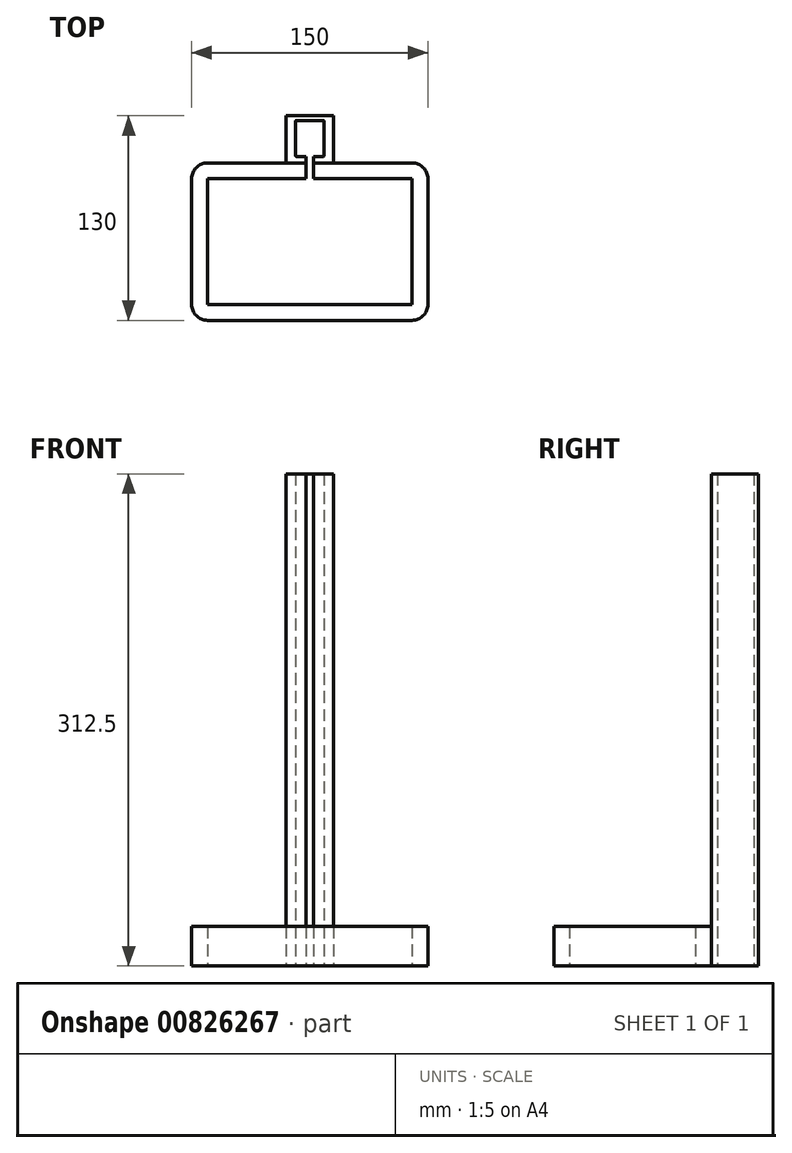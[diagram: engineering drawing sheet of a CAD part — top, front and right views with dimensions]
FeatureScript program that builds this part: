
annotation { "Feature Type Name" : "Feature", "Feature Type Description" : "" }
export const myFeature = defineFeature(function(context is Context, id is Id, definition is map)
    precondition{}
    {
        {
            var Q0;
            Q0=qCreatedBy(makeId("Top.planeOp"),FACE);
            var sketch = newSketch(context, id + "F0", { "sketchPlane" : qUnion([Q0])});
            skLineSegment(sketch, "E0.bottom", {"start": v(-65, 50) * mm, "end": v(65, 50) * mm});
            skLineSegment(sketch, "E0.top", {"start": v(-65, -50) * mm, "end": v(65, -50) * mm});
            skLineSegment(sketch, "E0.left", {"start": v(-75, 40) * mm, "end": v(-75, -40) * mm});
            skLineSegment(sketch, "E0.right", {"start": v(75, 40) * mm, "end": v(75, -40) * mm});
            skLineSegment(sketch, "E1", {"start": v(0, 0) * mm, "end": v(-75, 0) * mm, "construction": true});
            skLineSegment(sketch, "E2", {"start": v(0, 0) * mm, "end": v(0, -50) * mm, "construction": true});
            skLineSegment(sketch, "E3.bottom", {"start": v(-15, 80) * mm, "end": v(15, 80) * mm});
            skLineSegment(sketch, "E3.top", {"start": v(-15, 50) * mm, "end": v(15, 50) * mm});
            skLineSegment(sketch, "E3.left", {"start": v(-15, 80) * mm, "end": v(-15, 50) * mm});
            skLineSegment(sketch, "E3.right", {"start": v(15, 80) * mm, "end": v(15, 50) * mm});
            skLineSegment(sketch, "E4", {"start": v(0, 0) * mm, "end": v(0, 80) * mm, "construction": true});
            skLineSegment(sketch, "E5.bottom", {"start": v(-65, 40) * mm, "end": v(65, 40) * mm});
            skLineSegment(sketch, "E5.top", {"start": v(-65, -40) * mm, "end": v(65, -40) * mm});
            skLineSegment(sketch, "E5.left", {"start": v(-65, 40) * mm, "end": v(-65, -40) * mm});
            skLineSegment(sketch, "E5.right", {"start": v(65, 40) * mm, "end": v(65, -40) * mm});
            skLineSegment(sketch, "E6.bottom", {"start": v(-2.5, 59.58) * mm, "end": v(2.5, 59.58) * mm});
            skLineSegment(sketch, "E6.top", {"start": v(-2.5, 40) * mm, "end": v(2.5, 40) * mm});
            skLineSegment(sketch, "E6.left", {"start": v(-2.5, 59.58) * mm, "end": v(-2.5, 40) * mm});
            skLineSegment(sketch, "E6.right", {"start": v(2.5, 59.58) * mm, "end": v(2.5, 40) * mm});
            skLineSegment(sketch, "E7", {"start": v(0, 0) * mm, "end": v(-65, 0) * mm, "construction": true});
            skPoint(sketch, "E8.visualSharp", {"position": v(-75, 50) * mm});
            skArc(sketch, "E8.filletArc", {"start": v(-65, 50) * mm, "mid": v(-72.07, 47.07) * mm, "end": v(-75, 40) * mm});
            skPoint(sketch, "E9.visualSharp", {"position": v(75, 50) * mm});
            skArc(sketch, "E9.filletArc", {"start": v(75, 40) * mm, "mid": v(72.07, 47.07) * mm, "end": v(65, 50) * mm});
            skPoint(sketch, "E10.visualSharp", {"position": v(-75, -50) * mm});
            skArc(sketch, "E10.filletArc", {"start": v(-75, -40) * mm, "mid": v(-72.07, -47.07) * mm, "end": v(-65, -50) * mm});
            skPoint(sketch, "E11.visualSharp", {"position": v(75, -50) * mm});
            skArc(sketch, "E11.filletArc", {"start": v(65, -50) * mm, "mid": v(72.07, -47.07) * mm, "end": v(75, -40) * mm});
            skLineSegment(sketch, "E12", {"start": v(0, 0) * mm, "end": v(0, 40) * mm});
            skCircle(sketch, "E13", {"center": v(0, 69.7) * mm, "radius": 6 * mm});
            skLineSegment(sketch, "E14", {"start": v(-9, 54) * mm, "end": v(-9, 77) * mm});
            skLineSegment(sketch, "E15", {"start": v(-9, 77) * mm, "end": v(9, 77) * mm});
            skLineSegment(sketch, "E16", {"start": v(0, 79.25) * mm, "end": v(0, 80) * mm});
            skLineSegment(sketch, "E17", {"start": v(-9, 54) * mm, "end": v(9, 54) * mm});
            skLineSegment(sketch, "E18", {"start": v(9, 54) * mm, "end": v(9, 77) * mm});
            skLineSegment(sketch, "E19", {"start": v(0, 77) * mm, "end": v(0, 80) * mm});
            skSolve(sketch);
        }
        {
            var Q0;
            Q0=makeQuery(id+"F0.imprint","IMPRINT",FACE,{"disambiguationData":[TD([[makeQuery(id+"F0.imprint","IMPRINT",EDGE,{"derivedFrom":sQuery(id+"F0.wireOp",EDGE,"E0.top")}),1.0]])]});
            var Q1;
            {var subQ5=sQuery(id+"F0.wireOp",EDGE,"E6.top");Q1=makeQuery(id+"F0.imprint","IMPRINT",FACE,{"disambiguationData":[TD([[makeQuery(id+"F0.imprint","IMPRINT",EDGE,{"derivedFrom":subQ5}),1.0]])]});}
            var Q2;
            {var subQ0=sQuery(id+"F0.wireOp",EDGE,"l1MtYh9c-CzXV-YJr5-94RZ-eUTwZ6HwwpDR");Q2=makeQuery(id+"F0.imprint","IMPRINT",FACE,{"disambiguationData":[TD([[makeQuery(id+"F0.imprint","IMPRINT",EDGE,{"derivedFrom":subQ0}),1.0]])]});}
            extrude(context, id + "F1", {"entities" : qUnion([Q0, Q1, Q2]), "endBound" : BoundingType.SYMMETRIC, "depth" : 25 * mm, "offsetDistance" : 25 * mm});
        }
        {
            var Q0;
            Q0=makeQuery(id+"F0.imprint","IMPRINT",FACE,{"disambiguationData":[TD([[makeQuery(id+"F0.imprint","IMPRINT",EDGE,{"derivedFrom":sQuery(id+"F0.wireOp",EDGE,"E3.bottom")}),-1.0]])]});
            var Q1;
            {var subQ0=sQuery(id+"F0.wireOp",EDGE,"iEGK5Bb7-SoDk-IzIK-Jkqt-TQqyKEJhDGZO");Q1=makeQuery(id+"F0.imprint","IMPRINT",FACE,{"disambiguationData":[TD([[makeQuery(id+"F0.imprint","IMPRINT",EDGE,{"derivedFrom":subQ0}),1.0]])]});}
            extrude(context, id + "F2", {"entities" : qUnion([Q0, Q1]), "operationType" : NewBodyOperationType.ADD, "depth" : 300 * mm, "offsetDistance" : 25 * mm, "hasSecondDirection" : true, "secondDirectionOppositeDirection" : true, "secondDirectionDepth" : 12.5 * mm});
        }
        {
            var Q0;
            Q0=makeQuery(id+"F0.imprint","IMPRINT",FACE,{"disambiguationData":[TD([[makeQuery(id+"F0.imprint","IMPRINT",EDGE,{"derivedFrom":sQuery(id+"F0.wireOp",EDGE,"E13")}),1.0]])]});
            extrude(context, id + "F3", {"entities" : qUnion([Q0]), "operationType" : NewBodyOperationType.REMOVE, "depth" : 50 * mm, "offsetDistance" : 25 * mm});
        }
        {
            var Q0;
            Q0=makeQuery(id+"F2.opExtrude","SWEPT_EDGE",EDGE,{"disambiguationData":[OSD([sQuery(id+"F0.wireOp",EDGE,"E14"),sQuery(id+"F0.wireOp",EDGE,"E15")])]});
            var Q1;
            Q1=makeQuery(id+"F2.opExtrude","SWEPT_EDGE",EDGE,{"disambiguationData":[OSD([sQuery(id+"F0.wireOp",EDGE,"E15"),sQuery(id+"F0.wireOp",EDGE,"E18")])]});
            var Q2;
            Q2=makeQuery(id+"F2.opExtrude","SWEPT_EDGE",EDGE,{"disambiguationData":[OSD([sQuery(id+"F0.wireOp",EDGE,"E14"),sQuery(id+"F0.wireOp",EDGE,"E17")])]});
            var Q3;
            Q3=makeQuery(id+"F2.opExtrude","SWEPT_EDGE",EDGE,{"disambiguationData":[OSD([sQuery(id+"F0.wireOp",EDGE,"E17"),sQuery(id+"F0.wireOp",EDGE,"E18")])]});
            fillet(context, id + "F4", {"entities" : qUnion([Q0, Q1, Q2, Q3]), "radius" : 0.5 * mm, "tangentPropagation" : true, "allowEdgeOverflow" : false});
        }
    });
